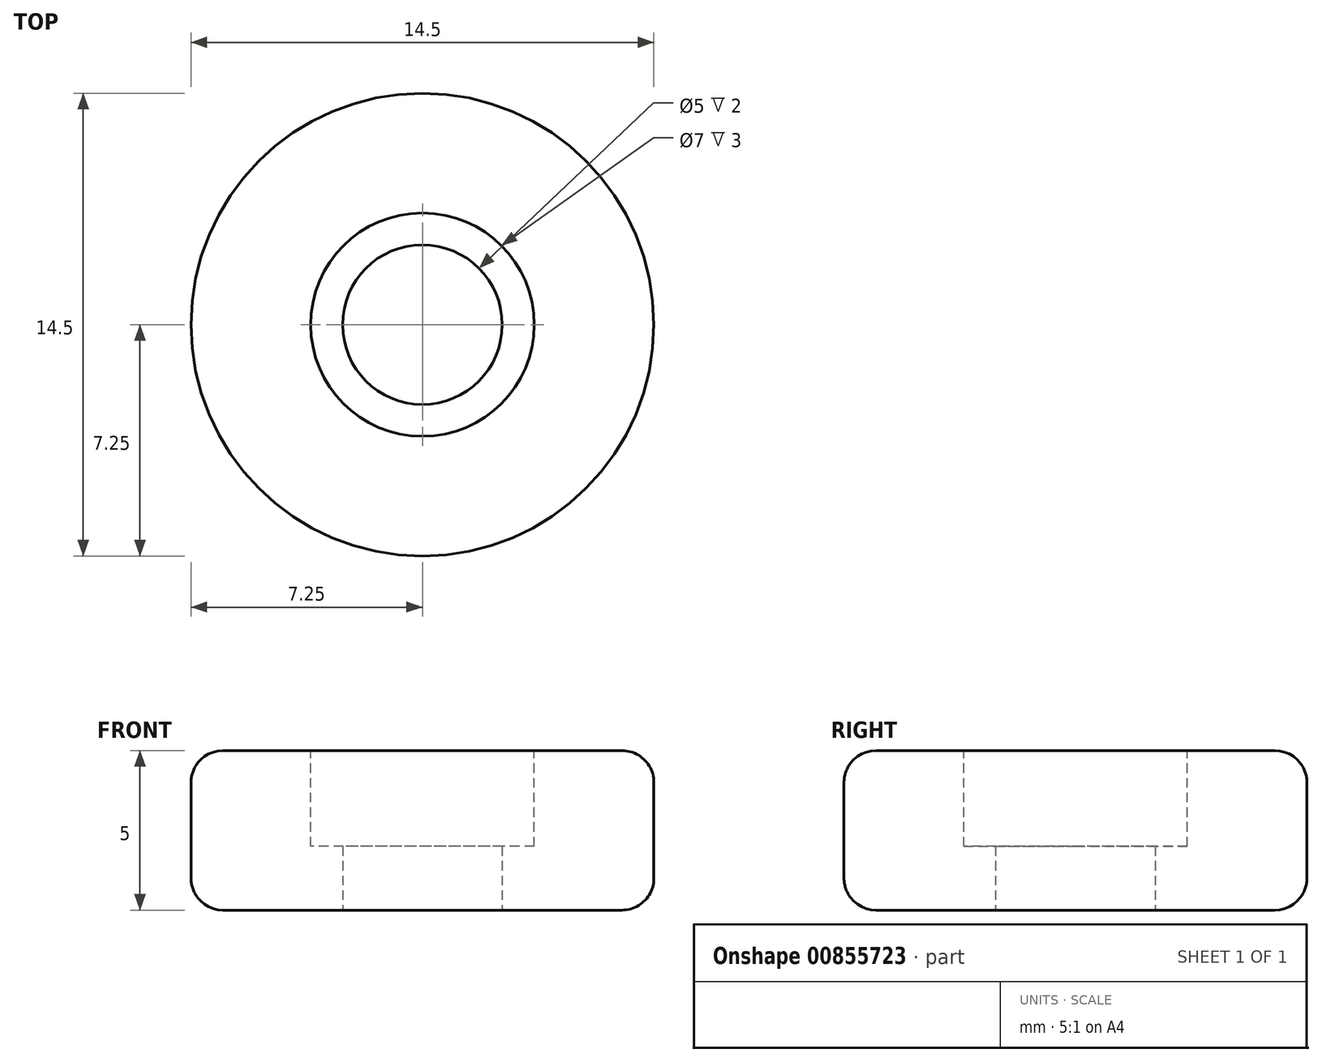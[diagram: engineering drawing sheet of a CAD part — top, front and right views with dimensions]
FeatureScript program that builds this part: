
annotation { "Feature Type Name" : "Feature", "Feature Type Description" : "" }
export const myFeature = defineFeature(function(context is Context, id is Id, definition is map)
    precondition{}
    {
        {
            var Q0;
            Q0=qCreatedBy(makeId("Top.planeOp"),FACE);
            var sketch = newSketch(context, id + "F0", { "sketchPlane" : qUnion([Q0])});
            skCircle(sketch, "E0", {"center": v(0, 0) * mm, "radius": 7.25 * mm});
            skCircle(sketch, "E1", {"center": v(0, 0) * mm, "radius": 2.5 * mm});
            skSolve(sketch);
        }
        {
            var Q0;
            Q0=makeQuery(id+"F0.imprint","IMPRINT",FACE,{"disambiguationData":[TD([[makeQuery(id+"F0.imprint","IMPRINT",EDGE,{"derivedFrom":sQuery(id+"F0.wireOp",EDGE,"E0")}),1.0]])]});
            extrude(context, id + "F1", {"entities" : qUnion([Q0]), "depth" : 5 * mm, "offsetDistance" : 25 * mm});
        }
        {
            var Q0;
            Q0=makeQuery(id+"F1.opExtrude","CAP_FACE",FACE,{"disambiguationData":[OSD([sQuery(id+"F0.wireOp",EDGE,"E0"),sQuery(id+"F0.wireOp",EDGE,"E1")])],"isStart":false});
            var sketch = newSketch(context, id + "F2", { "sketchPlane" : qUnion([Q0])});
            skCircle(sketch, "E2", {"center": v(0, 0) * mm, "radius": 3.5 * mm});
            skSolve(sketch);
        }
        {
            var Q0;
            Q0=makeQuery(id+"F2.imprint","IMPRINT",FACE,{"disambiguationData":[TD([[makeQuery(id+"F2.imprint","IMPRINT",EDGE,{"derivedFrom":sQuery(id+"F2.wireOp",EDGE,"E2")}),1.0]])]});
            extrude(context, id + "F3", {"entities" : qUnion([Q0]), "operationType" : NewBodyOperationType.REMOVE, "oppositeDirection" : true, "depth" : 3 * mm, "offsetDistance" : 25 * mm});
        }
        {
            var Q0;
            Q0=makeQuery(id+"F1.opExtrude","CAP_EDGE",EDGE,{"disambiguationData":[OSD([sQuery(id+"F0.wireOp",EDGE,"E0")])],"isStart":false});
            var Q1;
            Q1=makeQuery(id+"F3.boolean.opBoolean","COPY",EDGE,{"derivedFrom":makeQuery(id+"F3.opExtrude","CAP_EDGE",EDGE,{"disambiguationData":[OSD([sQuery(id+"F2.wireOp",EDGE,"E2")])],"isStart":true})});
            var Q2;
            Q2=makeQuery(id+"F1.opExtrude","CAP_EDGE",EDGE,{"disambiguationData":[OSD([sQuery(id+"F0.wireOp",EDGE,"E0")])],"isStart":true});
            fillet(context, id + "F4", {"entities" : qUnion([Q0, Q1, Q2]), "radius" : 1 * mm, "tangentPropagation" : true, "allowEdgeOverflow" : false});
        }
    });
